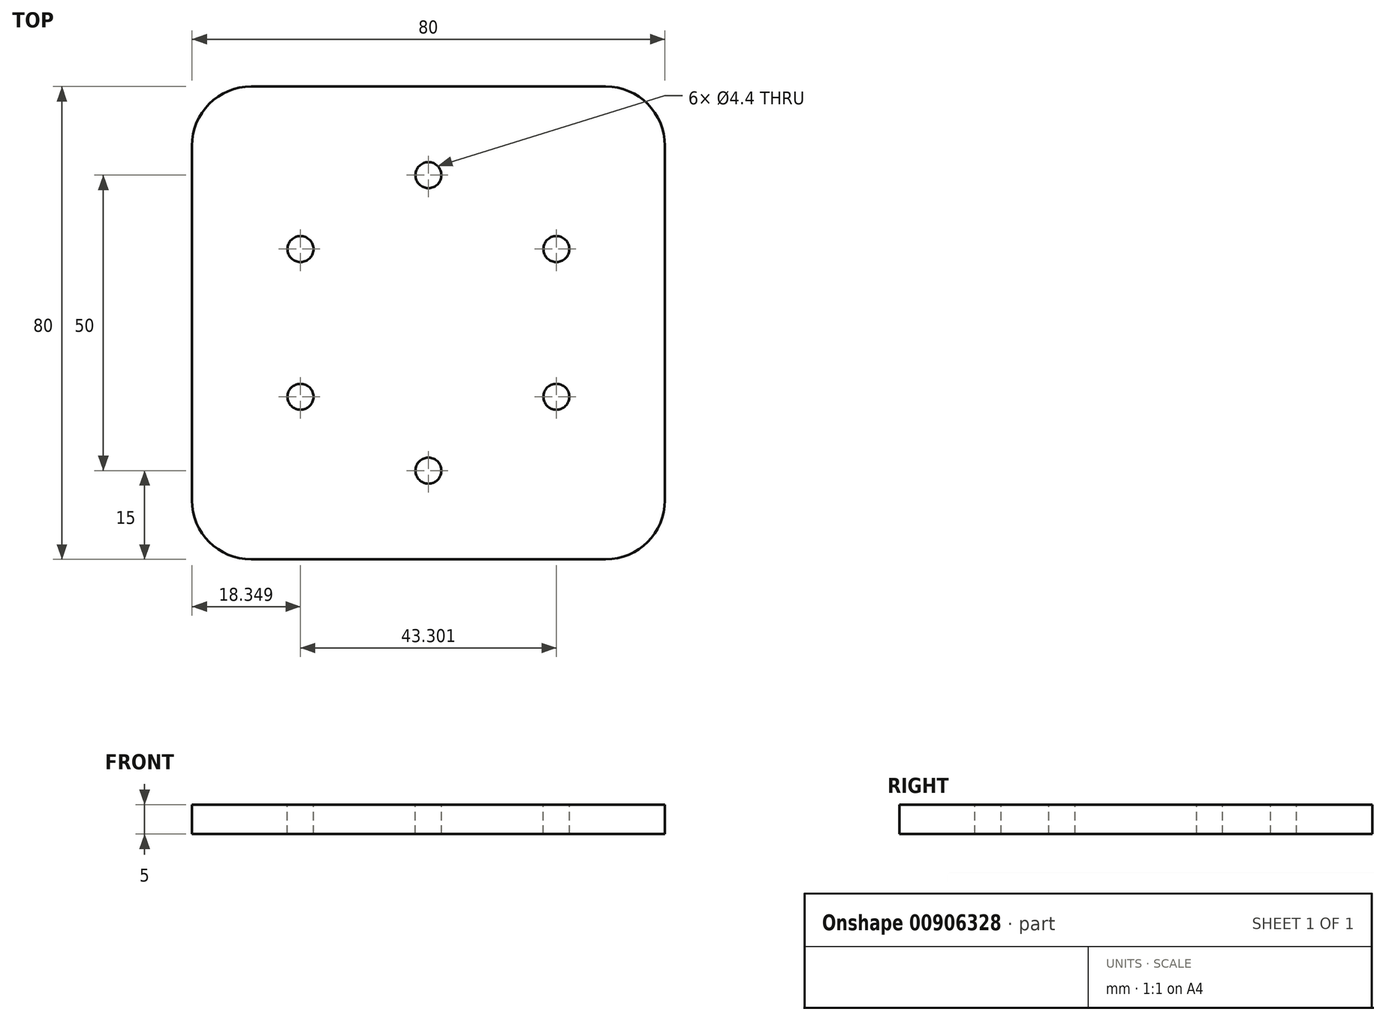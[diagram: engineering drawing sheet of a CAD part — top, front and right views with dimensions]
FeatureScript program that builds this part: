
annotation { "Feature Type Name" : "Feature", "Feature Type Description" : "" }
export const myFeature = defineFeature(function(context is Context, id is Id, definition is map)
    precondition{}
    {
        {
            var Q0;
            Q0=qCreatedBy(makeId("Top.planeOp"),FACE);
            var sketch = newSketch(context, id + "F0", { "sketchPlane" : qUnion([Q0])});
            skLineSegment(sketch, "E0.bottom", {"start": v(40, 40) * mm, "end": v(-40, 40) * mm});
            skLineSegment(sketch, "E0.top", {"start": v(40, -40) * mm, "end": v(-40, -40) * mm});
            skLineSegment(sketch, "E0.left", {"start": v(40, 40) * mm, "end": v(40, -40) * mm});
            skLineSegment(sketch, "E0.right", {"start": v(-40, 40) * mm, "end": v(-40, -40) * mm});
            skPoint(sketch, "E0.middle", {"position": v(0, 0) * mm});
            skSolve(sketch);
        }
        {
            var Q0;
            Q0=makeQuery(id+"F0.imprint","IMPRINT",FACE,{"disambiguationData":[TD([[makeQuery(id+"F0.imprint","IMPRINT",EDGE,{"derivedFrom":sQuery(id+"F0.wireOp",EDGE,"E0.bottom")}),1.0]])]});
            extrude(context, id + "F1", {"entities" : qUnion([Q0]), "depth" : 5 * mm, "offsetDistance" : 25 * mm});
        }
        {
            var Q0;
            Q0=makeQuery(id+"F1.opExtrude","CAP_FACE",FACE,{"disambiguationData":[OSD([sQuery(id+"F0.wireOp",EDGE,"E0.bottom"),sQuery(id+"F0.wireOp",EDGE,"E0.top"),sQuery(id+"F0.wireOp",EDGE,"E0.left"),sQuery(id+"F0.wireOp",EDGE,"E0.right")])],"isStart":false});
            var sketch = newSketch(context, id + "F2", { "sketchPlane" : qUnion([Q0])});
            skPoint(sketch, "E1", {"position": v(0, 25) * mm});
            skPoint(sketch, "E2.1.0", {"position": v(-21.65, 12.5) * mm});
            skPoint(sketch, "E2.2.0", {"position": v(-21.65, -12.5) * mm});
            skPoint(sketch, "E2.3.0", {"position": v(0, -25) * mm});
            skPoint(sketch, "E2.4.0", {"position": v(21.65, -12.5) * mm});
            skPoint(sketch, "E2.5.0", {"position": v(21.65, 12.5) * mm});
            skPoint(sketch, "E2.center", {"position": v(0, 0) * mm});
            skSolve(sketch);
        }
        {
            var Q0;
            Q0=sQuery(id+"F2.wireOp",VERTEX,"E1");
            var Q1;
            Q1=sQuery(id+"F2.wireOp",VERTEX,"E2.5.0");
            var Q2;
            Q2=sQuery(id+"F2.wireOp",VERTEX,"E2.4.0");
            var Q3;
            Q3=sQuery(id+"F2.wireOp",VERTEX,"E2.3.0");
            var Q4;
            Q4=sQuery(id+"F2.wireOp",VERTEX,"E2.2.0");
            var Q5;
            Q5=sQuery(id+"F2.wireOp",VERTEX,"E2.1.0");
            var Q6;
            Q6=makeQuery(id+"F1.opExtrude","SWEPT_BODY",BODY,{"disambiguationData":[OSD([sQuery(id+"F0.wireOp",EDGE,"E0.bottom"),sQuery(id+"F0.wireOp",EDGE,"E0.top"),sQuery(id+"F0.wireOp",EDGE,"E0.left"),sQuery(id+"F0.wireOp",EDGE,"E0.right")])]});
            hole(context, id + "F3", {"style" : HoleStyle.SIMPLE, "endStyle" : HoleEndStyle.THROUGH, "holeDiameter" : 4.4 * mm, "majorDiameter" : 5 * mm, "isTappedThrough" : true, "tappedDepth" : 12 * mm, "tapClearance" : 3, "locations" : qUnion([Q0, Q1, Q2, Q3, Q4, Q5]), "scope" : qUnion([Q6])});
        }
        {
            var Q0;
            Q0=makeQuery(id+"F1.opExtrude","SWEPT_EDGE",EDGE,{"disambiguationData":[OSD([sQuery(id+"F0.wireOp",EDGE,"E0.top"),sQuery(id+"F0.wireOp",EDGE,"E0.left")])]});
            var Q1;
            Q1=makeQuery(id+"F1.opExtrude","SWEPT_EDGE",EDGE,{"disambiguationData":[OSD([sQuery(id+"F0.wireOp",EDGE,"E0.bottom"),sQuery(id+"F0.wireOp",EDGE,"E0.left")])]});
            var Q2;
            Q2=makeQuery(id+"F1.opExtrude","SWEPT_EDGE",EDGE,{"disambiguationData":[OSD([sQuery(id+"F0.wireOp",EDGE,"E0.top"),sQuery(id+"F0.wireOp",EDGE,"E0.right")])]});
            var Q3;
            Q3=makeQuery(id+"F1.opExtrude","SWEPT_EDGE",EDGE,{"disambiguationData":[OSD([sQuery(id+"F0.wireOp",EDGE,"E0.bottom"),sQuery(id+"F0.wireOp",EDGE,"E0.right")])]});
            fillet(context, id + "F4", {"entities" : qUnion([Q0, Q1, Q2, Q3]), "radius" : 10 * mm, "tangentPropagation" : true, "allowEdgeOverflow" : false});
        }
    });
